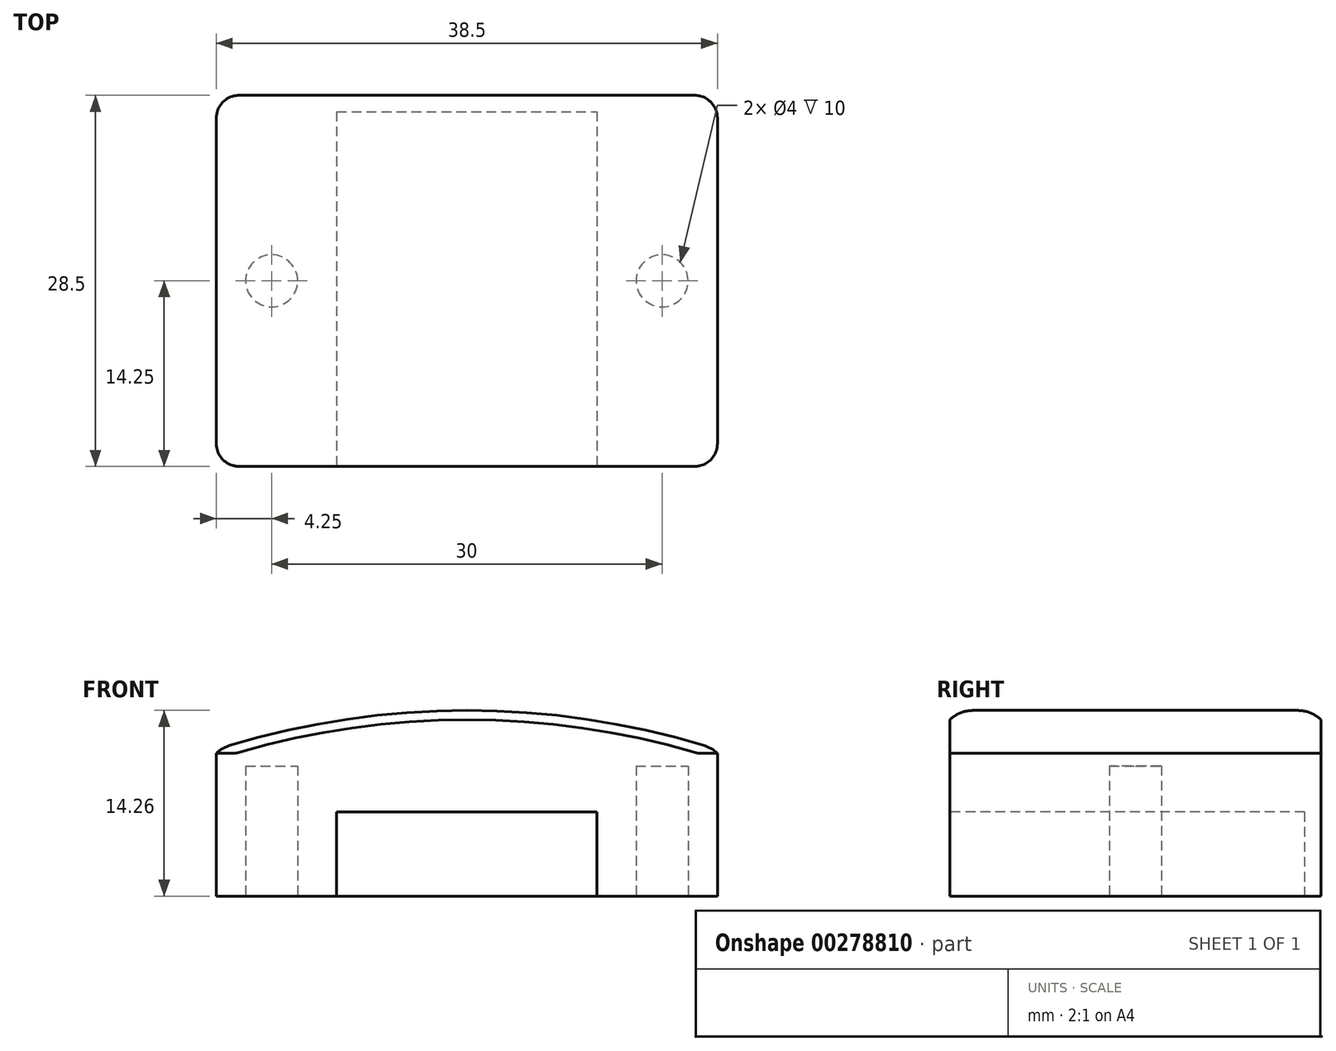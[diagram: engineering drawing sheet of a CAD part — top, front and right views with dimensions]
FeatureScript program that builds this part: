
annotation { "Feature Type Name" : "Feature", "Feature Type Description" : "" }
export const myFeature = defineFeature(function(context is Context, id is Id, definition is map)
    precondition{}
    {
        {
            var Q0;
            Q0=qCreatedBy(makeId("Front.planeOp"),FACE);
            var sketch = newSketch(context, id + "F0", { "sketchPlane" : qUnion([Q0])});
            skLineSegment(sketch, "E0", {"start": v(0, 0) * mm, "end": v(0, 63) * mm, "construction": true});
            skArc(sketch, "E1", {"start": v(20, 59.74) * mm, "mid": v(0, 63) * mm, "end": v(-20, 59.74) * mm});
            skLineSegment(sketch, "E2", {"start": v(-20, 59.74) * mm, "end": v(-20, 48.74) * mm});
            skLineSegment(sketch, "E3", {"start": v(-20, 48.74) * mm, "end": v(20, 48.74) * mm});
            skLineSegment(sketch, "E4", {"start": v(20, 48.74) * mm, "end": v(20, 59.74) * mm});
            skSolve(sketch);
        }
        {
            var Q0;
            Q0=qSketchRegion(id+"F0",true);
            extrude(context, id + "F1", {"entities" : qUnion([Q0]), "endBound" : BoundingType.SYMMETRIC, "depth" : 30 * mm});
        }
        {
            var Q0;
            Q0=qCreatedBy(makeId("Front.planeOp"),FACE);
            var sketch = newSketch(context, id + "F2", { "sketchPlane" : qUnion([Q0])});
            skLineSegment(sketch, "E5", {"start": v(0, 0) * mm, "end": v(0, 69.67) * mm, "construction": true});
            skArc(sketch, "E6.0", {"start": v(20, 59.74) * mm, "mid": v(0, 63) * mm, "end": v(-20, 59.74) * mm, "construction": true});
            skLineSegment(sketch, "E7.bottom", {"start": v(10, 55.2) * mm, "end": v(-10, 55.2) * mm});
            skLineSegment(sketch, "E7.top", {"start": v(10, 0) * mm, "end": v(-10, 0) * mm});
            skLineSegment(sketch, "E7.left", {"start": v(10, 55.2) * mm, "end": v(10, 0) * mm});
            skLineSegment(sketch, "E7.right", {"start": v(-10, 55.2) * mm, "end": v(-10, 0) * mm});
            skPoint(sketch, "E7.middle", {"position": v(0, 27.6) * mm});
            skLineSegment(sketch, "E8", {"start": v(-10, 55.2) * mm, "end": v(-10, 62.2) * mm, "construction": true});
            skSolve(sketch);
        }
        {
            var Q0;
            Q0 = qSketchRegion(id + "F2", true);
            extrude(context, id + "F3", {"entities" : qUnion([Q0]), "operationType" : NewBodyOperationType.REMOVE, "endBound" : BoundingType.SYMMETRIC, "oppositeDirection" : true, "depth" : 26 * mm});
        }
        {
            var Q0;
            Q0=makeQuery(id+"F1.opExtrude","SWEPT_FACE",FACE,{"disambiguationData":[OSD([sQuery(id+"F0.wireOp",EDGE,"E3")])]});
            var sketch = newSketch(context, id + "F4", { "sketchPlane" : qUnion([Q0])});
            skLineSegment(sketch, "E9", {"start": v(-20, 0) * mm, "end": v(20, 0) * mm, "construction": true});
            skLineSegment(sketch, "E10", {"start": v(0, 0) * mm, "end": v(0, -20.7) * mm, "construction": true});
            skPoint(sketch, "E10.endSnap0", {"position": v(0, -15) * mm});
            skCircle(sketch, "E11", {"center": v(-15, 0) * mm, "radius": 2 * mm});
            skCircle(sketch, "E12.MirrorC", {"center": v(15, 0) * mm, "radius": 2 * mm});
            skSolve(sketch);
        }
        {
            var Q0;
            Q0 = qSketchRegion(id + "F4", true);
            extrude(context, id + "F5", {"entities" : qUnion([Q0]), "operationType" : NewBodyOperationType.REMOVE, "oppositeDirection" : true, "depth" : 10 * mm});
        }
        {
            var Q0;
            Q0=makeQuery(id+"F1.opExtrude","CAP_EDGE",EDGE,{"disambiguationData":[OSD([sQuery(id+"F0.wireOp",EDGE,"E2")])],"isStart":false});
            var Q1;
            Q1=makeQuery(id+"F1.opExtrude","CAP_EDGE",EDGE,{"disambiguationData":[OSD([sQuery(id+"F0.wireOp",EDGE,"E2")])],"isStart":true});
            var Q2;
            Q2=makeQuery(id+"F1.opExtrude","CAP_EDGE",EDGE,{"disambiguationData":[OSD([sQuery(id+"F0.wireOp",EDGE,"E4")])],"isStart":false});
            var Q3;
            Q3=makeQuery(id+"F1.opExtrude","CAP_EDGE",EDGE,{"disambiguationData":[OSD([sQuery(id+"F0.wireOp",EDGE,"E4")])],"isStart":true});
            var Q4;
            Q4=makeQuery(id+"F1.opExtrude","SWEPT_EDGE",EDGE,{"disambiguationData":[OSD([sQuery(id+"F0.wireOp",EDGE,"E1"),sQuery(id+"F0.wireOp",EDGE,"E4")])]});
            var Q5;
            Q5=makeQuery(id+"F1.opExtrude","CAP_EDGE",EDGE,{"disambiguationData":[OSD([sQuery(id+"F0.wireOp",EDGE,"E1")])],"isStart":false});
            var Q6;
            Q6=makeQuery(id+"F1.opExtrude","CAP_EDGE",EDGE,{"disambiguationData":[OSD([sQuery(id+"F0.wireOp",EDGE,"E1")])],"isStart":true});
            var Q7;
            Q7=makeQuery(id+"F1.opExtrude","SWEPT_EDGE",EDGE,{"disambiguationData":[OSD([sQuery(id+"F0.wireOp",EDGE,"E1"),sQuery(id+"F0.wireOp",EDGE,"E2")])]});
            fillet(context, id + "F6", {"entities" : qUnion([Q0, Q1, Q2, Q3, Q4, Q5, Q6, Q7]), "radius" : 2.5 * mm, "tangentPropagation" : true, "allowEdgeOverflow" : false});
        }
        {
            var Q0;
            Q0=makeQuery(id+"F1.opExtrude","SWEPT_FACE",FACE,{"disambiguationData":[OSD([sQuery(id+"F0.wireOp",EDGE,"E3")])]});
            var sketch = newSketch(context, id + "F7", { "sketchPlane" : qUnion([Q0])});
            skLineSegment(sketch, "E13.0", {"start": v(-17.5, 15) * mm, "end": v(17.5, 15) * mm});
            skArc(sketch, "E13.1", {"start": v(-17.5, 15) * mm, "mid": v(-19.27, 14.27) * mm, "end": v(-20, 12.5) * mm});
            skLineSegment(sketch, "E13.2", {"start": v(-20, 12.5) * mm, "end": v(-20, -12.5) * mm});
            skArc(sketch, "E13.3", {"start": v(-20, -12.5) * mm, "mid": v(-19.27, -14.27) * mm, "end": v(-17.5, -15) * mm});
            skLineSegment(sketch, "E13.4", {"start": v(-17.5, -15) * mm, "end": v(17.5, -15) * mm});
            skArc(sketch, "E13.5", {"start": v(17.5, -15) * mm, "mid": v(19.27, -14.27) * mm, "end": v(20, -12.5) * mm});
            skLineSegment(sketch, "E13.6", {"start": v(20, 12.5) * mm, "end": v(20, -12.5) * mm});
            skArc(sketch, "E13.7", {"start": v(20, 12.5) * mm, "mid": v(19.27, 14.27) * mm, "end": v(17.5, 15) * mm});
            skLineSegment(sketch, "E14.0", {"start": v(-19.25, 12.5) * mm, "end": v(-19.25, -12.5) * mm});
            skArc(sketch, "E14.1", {"start": v(-17.5, 14.25) * mm, "mid": v(-18.74, 13.74) * mm, "end": v(-19.25, 12.5) * mm});
            skArc(sketch, "E14.2", {"start": v(-19.25, -12.5) * mm, "mid": v(-18.74, -13.74) * mm, "end": v(-17.5, -14.25) * mm});
            skLineSegment(sketch, "E14.3", {"start": v(-17.5, 14.25) * mm, "end": v(17.5, 14.25) * mm});
            skLineSegment(sketch, "E14.4", {"start": v(-17.5, -14.25) * mm, "end": v(17.5, -14.25) * mm});
            skArc(sketch, "E14.5", {"start": v(17.5, -14.25) * mm, "mid": v(18.74, -13.74) * mm, "end": v(19.25, -12.5) * mm});
            skLineSegment(sketch, "E14.6", {"start": v(19.25, 12.5) * mm, "end": v(19.25, -12.5) * mm});
            skArc(sketch, "E14.7", {"start": v(19.25, 12.5) * mm, "mid": v(18.74, 13.74) * mm, "end": v(17.5, 14.25) * mm});
            skSolve(sketch);
        }
        {
            var Q0;
            Q0 = qSketchRegion(id + "F7", true);
            extrude(context, id + "F8", {"entities" : qUnion([Q0]), "operationType" : NewBodyOperationType.REMOVE, "endBound" : BoundingType.THROUGH_ALL, "oppositeDirection" : true, "depth" : 25 * mm});
        }
        {
            var Q0;
            Q0=makeQuery(id+"F3.boolean.opBoolean","COPY",FACE,{"derivedFrom":makeQuery(id+"F3.opExtrude","CAP_FACE",FACE,{"disambiguationData":[OSD([sQuery(id+"F2.wireOp",EDGE,"E7.bottom"),sQuery(id+"F2.wireOp",EDGE,"E7.top"),sQuery(id+"F2.wireOp",EDGE,"E7.left"),sQuery(id+"F2.wireOp",EDGE,"E7.right")])],"isStart":true})});
            extrude(context, id + "F9", {"entities" : qUnion([Q0]), "operationType" : NewBodyOperationType.REMOVE, "endBound" : BoundingType.THROUGH_ALL, "oppositeDirection" : true, "depth" : 25 * mm});
        }
    });
